# Revit family: (VRUD) Vicky RingUp & Downward Light Acoustic Light -
name_source: partatom
category: Lighting Fixtures
units: mm (PartAtom-declared; Revit-internal decimal feet)

## family parameters
Cut with Voids When Loaded = No
Host = Face
Light Source = Yes
Part Type = Normal
Room Calculation Point = No
Round Connector Dimension = Use Diameter
Shared = No

## types (7) — shared parameters
Average life based on 77F(HRS) = 50000
CRI = 90
Canopy Height = 0' - 2"
Color Filter = 16777215
Description = The Vicky Ring light is a unique ring-style light with an LED light source illuminating up & downward
Dimming / Control = 0-10V
Dimming Lamp Color Temperature Shift = <None>
Finish/Color = Aluminum
Fixture Height = 4' - 0"
Fixture Width = 0' - 0"
H2 = 3' - 9 15/32"
IP Rating = 20
Inside Body = No
Inside Body Material = <By Category>
Load Classification = Lighting
Manufacturer = Above All Lighting
Power Factor = 1
Tilt Angle = -90.00°
Type Comments = Ring Up & Downward Light Acoustic Light
URL = https://www.abovealllighting.com
Voltage = 120-277 V

## per-type parameters (varying)
| type | Apparent Load | B | B1 | B2 | D1 | D2 | Default Elevation | Fixture Diameter | H1 | Inner Diameter | Model | Order number | Photometric Web File | Wattage Comments |
| VRUD-13559-30901-ACPMK-WH | 169 VA | 0' - 3 1/2" | 2' - 5 11/32" | 2' - 1 27/32" | 0' - 5" | 0' - 3 1/2" | 0' - 3 1/2" | 4' - 11 3/32" | 4' - 4 5/16" | 2' - 4 1/4" | VRUD-13559-40901-ACPMK-WH | 16330 | VRUD-13559-30901.ies | 135 W |
| VRUD-8035-40901-ACPMK-WH | 100 VA | 0' - 3 1/2" | 1' - 5 1/2" | 1' - 2" | 0' - 5" | 0' - 3 1/2" | 0' - 0" | 2' - 11 13/32" | 3' - 11 19/32" | 1' - 4 13/32" | VRUD-8035-40901-ACPMK-WH | 16328 | VRUD-8035-40901.IES | 80 W |
| VRUD-12047-30901-ACPMK-WH | 150 VA | 0' - 3 1/2" | 1' - 11 13/32" | 1' - 7 29/32" | 0' - 5" | 0' - 3 1/2" | 0' - 0" | 3' - 11 3/16" | 4' - 1 21/32" | 1' - 10 5/16" | VRUD-12047-40901-ACPMK-WH | 16329 | VRUD-12047-30901.ies | 120W |
| VRUD-6524-30901-ACPMK-WH | 81 VA | 0' - 3 1/2" | 0' - 11 19/32" | 0' - 8 3/32" | 0' - 5" | 0' - 3 1/2" | 0' - 0" | 1' - 11 19/32" | 3' - 10 3/16" | 0' - 10 1/2" | VRUD-6524-40901-ACPMK-WH | 16327 | VRUD-6524-30901.ies | 65 W |
| VRUD-15079-40901-ACPMK-WH | 188 VA | 0' - 5 1/2" | 3' - 3 7/32" | 2' - 9 23/32" | 0' - 7" | 0' - 5 1/2" | 0' - 3 1/2" | 6' - 6 13/16" | 4' - 8 19/32" | 3' - 2 3/32" | VRUD-15079-40901-ACPMK-WH | 16331 | generic.ies | 150W |
| VRUD-300118-40901-ACPMK-WH | 375 VA | 0' - 7 1/2" | 4' - 10 27/32" | 4' - 3 11/32" | 0' - 9" | 0' - 7 1/2" | 0' - 0" | 9' - 10 3/32" | 5' - 8 19/32" | 4' - 9 3/4" | VRUD-300118-40901-ACPMK-WH | 16332 | generic.ies | 300 W |
| VRUD-480197-40901-ACPMK-WH | 600 VA | 0' - 8 1/2" | 8' - 2 1/4" | 7' - 5 3/4" | 0' - 10" | 0' - 8 1/2" | 0' - 3 1/2" | 16' - 4 29/32" | 8' - 4 5/8" | 8' - 1 5/32" | VRUD-480197-40901-ACPMK-WH | 16333 | generic.ies | 480 W |

## geometry (parser evidence)
native form markers: Sweep x18
no freeform markers — native parametric forms only
